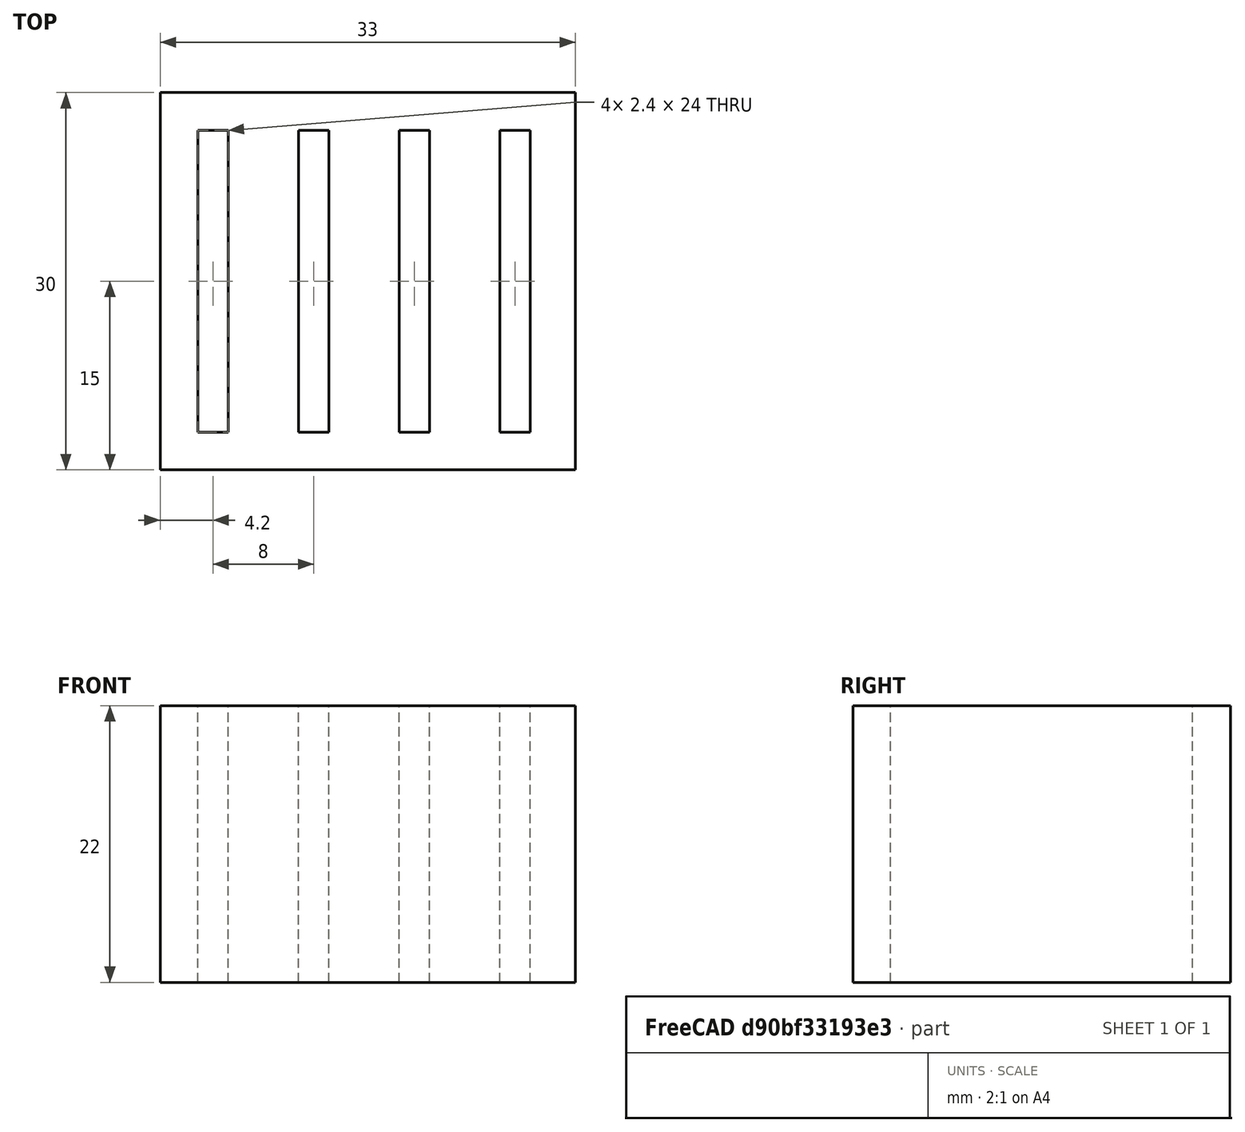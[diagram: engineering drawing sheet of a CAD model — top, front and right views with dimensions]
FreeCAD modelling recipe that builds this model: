
FCSTD DOCUMENT  (FreeCAD 0.21R33694 (Git))
Label: OJT1_T07R02-portaSDs
License: All rights reserved
LicenseURL: http://en.wikipedia.org/wiki/All_rights_reserved
objects: Part::Box×5, Part::MultiFuse×2, Part::Cut×1
note: 8 computed .brp shape members not serialized (recipe doc carries the construction recipe); baked Part::Feature solids carry a one-line shape summary decoded from their .brp

FEATURE [Part::Box] Box  label="Cub"
  AttacherType = Attacher::AttachEngine3D
  Height = 22
  Length = 33
  Placement = pos=(-3,-3,0) rot=(0,0,1;0rad)
  Width = 30
FEATURE [Part::Box] Box001  label="Cub001"
  AttacherType = Attacher::AttachEngine3D
  Height = 22
  Length = 2.4
  Width = 24
FEATURE [Part::Box] Box002  label="Cub002"
  AttacherType = Attacher::AttachEngine3D
  Height = 22
  Length = 2.4
  Placement = pos=(8,0,0) rot=(0,0,1;0rad)
  Width = 24
FEATURE [Part::Box] Box003  label="Cub003"
  AttacherType = Attacher::AttachEngine3D
  Height = 22
  Length = 2.4
  Placement = pos=(16,0,0) rot=(0,0,1;0rad)
  Width = 24
FEATURE [Part::Box] Box004  label="Cub004"
  AttacherType = Attacher::AttachEngine3D
  Height = 22
  Length = 2.4
  Placement = pos=(24,0,0) rot=(0,0,1;0rad)
  Width = 24
FEATURE [Part::MultiFuse] Fusion
  Refine = true
  Shapes = -> [Box001,Box002]
FEATURE [Part::MultiFuse] Fusion001
  Refine = true
  Shapes = -> [Box003,Box004,Fusion]
FEATURE [Part::Cut] Cut
  Base = -> Box
  Refine = true
  Tool = -> Fusion001
